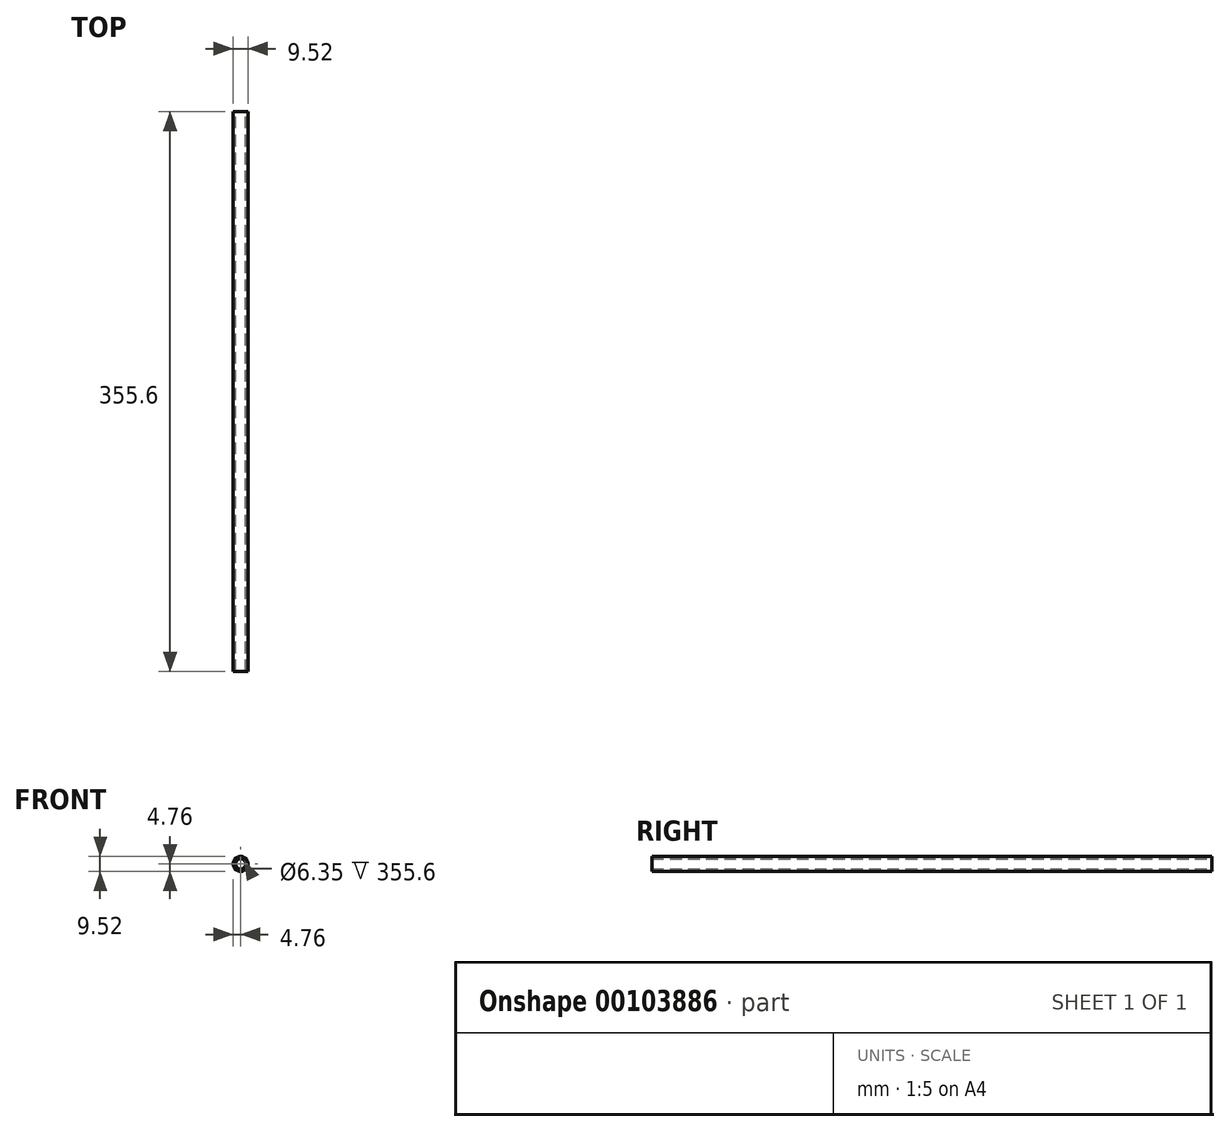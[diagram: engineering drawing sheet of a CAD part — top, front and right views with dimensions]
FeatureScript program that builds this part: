
annotation { "Feature Type Name" : "Feature", "Feature Type Description" : "" }
export const myFeature = defineFeature(function(context is Context, id is Id, definition is map)
    precondition{}
    {
        {
            var Q0;
            Q0=qCreatedBy(makeId("Front.planeOp"),FACE);
            var sketch = newSketch(context, id + "F0", { "sketchPlane" : qUnion([Q0])});
            skCircle(sketch, "E0", {"center": v(0, 0) * mm, "radius": 4.76 * mm});
            skCircle(sketch, "E1", {"center": v(0, 0) * mm, "radius": 3.18 * mm});
            skSolve(sketch);
        }
        {
            var Q0;
            Q0=makeQuery(id+"F0.imprint","IMPRINT",FACE,{"disambiguationData":[TD([[makeQuery(id+"F0.imprint","IMPRINT",EDGE,{"derivedFrom":sQuery(id+"F0.wireOp",EDGE,"E0")}),1.0]])]});
            extrude(context, id + "F1", {"entities" : qUnion([Q0]), "depth" : 355.6 * mm});
        }
    });
